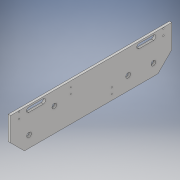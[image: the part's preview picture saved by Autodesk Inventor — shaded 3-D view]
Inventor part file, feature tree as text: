
AUTODESK INVENTOR PART (.ipt)
format: ipt  version: 2017 (Build 210142000, 142)  size: 202,240 bytes
history: native  units: in
note: dims shown in document units (in); Inventor stores cm internally (conversion verified against a paired STEP export)
features: extrude x5, sketch x5, projected_geometry x4, chamfer x2
ambient origin geometry x8: Origin, YZ Plane, XZ Plane, XY Plane, X Axis, Y Axis, Z Axis, Center Point
bodies: Solid1 (feature_tree)
feature tree (16):
  extrude  "Extrusion1"  Depth=17.5in
  chamfer  "Chamfer1"  Distance=0.25in
  chamfer  "Chamfer2"  Distance=1.5in Angle=45.0deg
  extrude  "Extrusion2"  Depth=0.5in TaperAngle=45.0deg
  extrude  "Extrusion3"  Depth=0.5in
  extrude  "Extrusion4"  Depth=0.5in
  extrude  "Extrusion5"  Depth=0.5in
  sketch  "Sketch1"  dims[d0=4.07in d1=17.5in]
  sketch  "Sketch2"  dims[d2=0.501in]
  projected_geometry  "Projected Loop1"
  sketch  "Sketch3"  dims[d3=1.25in]
  projected_geometry  "Projected Loop2"
  sketch  "Sketch4"  dims[d4=2.0in]
  projected_geometry  "Projected Loop3"
  sketch  "Sketch5"  dims[d5=2.0in d6=0.25in d7=0.0in d8=1.5in d9=0.125in d10=45.0deg d11=1.5in d12=0.125in d13=45.0deg d14=0.501in d15=4.741in d16=1.469in d17=0.501in d18=1.469in d19=4.741in d20=1.0in d21=0.0in d22=6.517in d23=0.125in d24=0.603in d25=0.125in d26=0.63in d27=6.517in d28=0.125in d29=0.603in d30=6.517in d31=0.125in d32=0.63in d33=6.517in d34=0.125in d35=6.517in d36=0.603in d37=0.125in d38=0.63in d39=0.125in d40=0.125in d41=0.603in d42=0.63in d43=6.517in d44=1.0in d45=0.0in d46=0.5in d47=1.975in d48=0.438in d49=0.5in d50=1.575in d57=1.0in d58=0.0in d59=0.155in d60=0.906in d61=0.094in d62=0.155in d64=0.155in d65=0.155in d66=0.094in d68=0.904in d69=1.0in d70=0.0in d71=0.781in d72=0.781in d73=0.5in d74=0.5in d75=1.975in d76=1.575in d77=0.438in]
  projected_geometry  "Projected Loop4"
